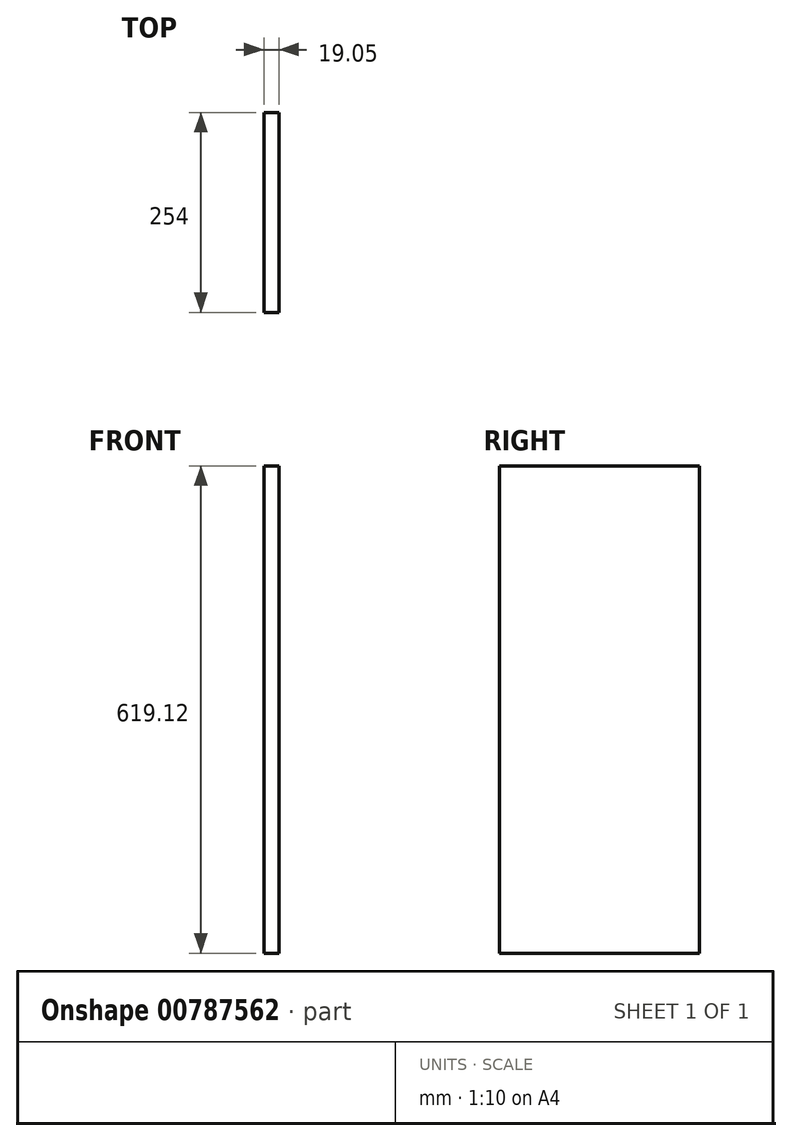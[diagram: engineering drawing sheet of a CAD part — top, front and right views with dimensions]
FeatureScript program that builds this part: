
annotation { "Feature Type Name" : "Feature", "Feature Type Description" : "" }
export const myFeature = defineFeature(function(context is Context, id is Id, definition is map)
    precondition{}
    {
        {
            var Q0;
            Q0=qCreatedBy(makeId("Right.planeOp"),FACE);
            var sketch = newSketch(context, id + "F0", { "sketchPlane" : qUnion([Q0])});
            skLineSegment(sketch, "E0.bottom", {"start": v(127, -309.56) * mm, "end": v(-127, -309.56) * mm});
            skLineSegment(sketch, "E0.top", {"start": v(127, 309.56) * mm, "end": v(-127, 309.56) * mm});
            skLineSegment(sketch, "E0.left", {"start": v(127, -309.56) * mm, "end": v(127, 309.56) * mm});
            skLineSegment(sketch, "E0.right", {"start": v(-127, -309.56) * mm, "end": v(-127, 309.56) * mm});
            skPoint(sketch, "E0.middle", {"position": v(0, 0) * mm});
            skSolve(sketch);
        }
        {
            var Q0;
            Q0 = qSketchRegion(id + "F0", true);
            extrude(context, id + "F1", {"entities" : qUnion([Q0]), "depth" : 19.05 * mm, "offsetDistance" : 25.4 * mm});
        }
    });
